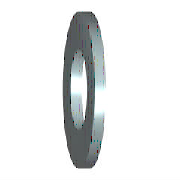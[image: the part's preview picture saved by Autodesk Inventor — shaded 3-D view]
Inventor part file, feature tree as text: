
AUTODESK INVENTOR PART (.ipt)
format: ipt  version: 2023.3 (Build 273359000, 359)  size: 106,496 bytes
history: native  units: mm (DEFAULTED — no unit token found)
features: extrude x1, other x1, plane x1, sketch x1
ambient origin geometry x7: Origin, YZ Plane, XY Plane, X Axis, Y Axis, Z Axis, Center Point
bodies: Solid1 (feature_tree)
feature tree (4):
  extrude  "Körper"  Depth=0.3mm
  other  "Work Axis1"
  plane  "Work Plane1"
  sketch  "Skizze"  dims[d0=2.4mm d1=5.0mm d2=0.3mm d3=0.0mm d4=0.0mm d5=0.0mm d6=0.0mm d7=0.0mm]
